# Revit family: Lighting_Fixture-Wall-Astro-Sparta
name_source: partatom
category: Lighting Fixtures
revit_build: Autodesk Revit 2014 (Build: 20130308_1515(x64)
units: mm (PartAtom-declared; Revit-internal decimal feet)

## types (2) — shared parameters
Assembly Code = D5020200
Casing Material = Astro - Aluminium - Chrome Finish
Class = 2
Color Filter = 16777215
Description = Mirror Light
Dimmable = No
Dimming Lamp Color Temperature Shift = <None>
Emit Shape Visible in Rendering = No
IP Rating = IP44
Lamp = LED
Lamp included = Yes
Length = 80 mm  [stored 0.262467 ft]
Light Source Elevation = 1600 mm  [stored 5.24934 ft]
Light Source From Wall = 60 mm  [stored 0.19685 ft]
Luminaire Lamp Efficiency Rating = -
Manufacturer = Astro Lighting Ltd, CM20 2DP
Mountable on normally flammable surfaces = Yes
Number of Poles = 1
Suitable for bathroom zone = Zones 2, 3
Tilt Angle = 90.00°
Type Comments = - Includes integral LED driver
-Can be mounted horizontally or vertically
URL = www.astrolighting.co.uk
Voltage = 230 V

## per-type parameters (varying)
| type | Apparent Load | Cable Entry Placer (from right) | Emit from Rectangle Length | Emit from Rectangle Width | Height | Model | Photometric Web File | Product Documentation | Wattage Comments | Weight | Width |
| 7162 Sparta 600 | 8 VA | 500 mm  [stored 1.64042 ft] | 29 mm  [stored 0.0951444 ft] | 592 mm  [stored 1.94226 ft] | 33 mm  [stored 0.108268 ft] | 7162 Sparta 600
Description: | 7162 SPARTA 600.ies | http://www.astrolighting.co.uk
/kw/sparta-600/7162_Sparta-600 | 7.2W | 1.13 kg | 600 mm  [stored 1.9685 ft] |
| 7163 Sparta 900 | 11 VA | 400 mm  [stored 1.31234 ft] | 28.6 mm | 892 mm | 32.6 mm | 7163 Sparta 900
Description: | 7163 SPARTA 900.ies | http://www.astrolighting.co.uk
/kw/7163/7163_Sparta-900 | 10.8W | 1.57 kg | 900 mm  [stored 2.95276 ft] |

note: [stored X ft] marks values corroborated as IEEE doubles in the binary element streams (Revit-internal decimal feet)

## geometry (parser evidence)
native form markers: Sweep x1
no freeform markers — native parametric forms only
